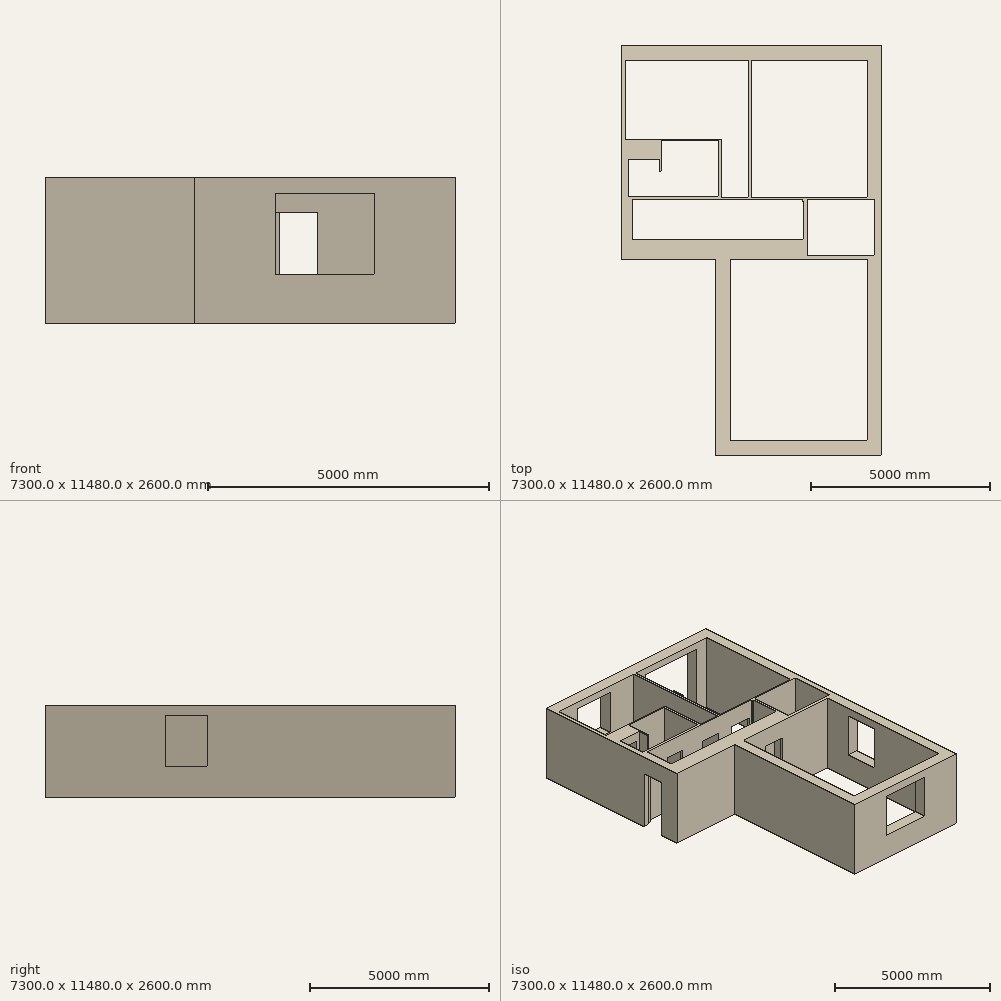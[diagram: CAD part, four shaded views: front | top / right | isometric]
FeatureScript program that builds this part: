
annotation { "Feature Type Name" : "Feature", "Feature Type Description" : "" }
export const myFeature = defineFeature(function(context is Context, id is Id, definition is map)
    precondition{}
    {
        {
            var Q0;
            Q0=qCreatedBy(makeId("Top.planeOp"),FACE);
            var sketch = newSketch(context, id + "F0", { "sketchPlane" : qUnion([Q0])});
            skLineSegment(sketch, "E0", {"start": v(-2650, 11480) * mm, "end": v(4650, 11480) * mm});
            skLineSegment(sketch, "E1", {"start": v(4650, 11480) * mm, "end": v(4650, 0) * mm});
            skLineSegment(sketch, "E2", {"start": v(4650, 0) * mm, "end": v(0, 0) * mm});
            skLineSegment(sketch, "E3", {"start": v(0, 0) * mm, "end": v(0, 5500) * mm});
            skLineSegment(sketch, "E4", {"start": v(0, 5500) * mm, "end": v(-2650, 5500) * mm});
            skLineSegment(sketch, "E5", {"start": v(-2650, 5500) * mm, "end": v(-2650, 11480) * mm});
            skLineSegment(sketch, "E6.bottom", {"start": v(4250, 410) * mm, "end": v(400, 410) * mm});
            skLineSegment(sketch, "E6.top", {"start": v(4250, 5500) * mm, "end": v(400, 5500) * mm});
            skLineSegment(sketch, "E6.left", {"start": v(4250, 410) * mm, "end": v(4250, 5500) * mm});
            skLineSegment(sketch, "E6.right", {"start": v(400, 410) * mm, "end": v(400, 5500) * mm});
            skLineSegment(sketch, "E7.bottom", {"start": v(4455, 5610) * mm, "end": v(2565, 5610) * mm});
            skLineSegment(sketch, "E7.top", {"start": v(4455, 7160) * mm, "end": v(2565, 7160) * mm});
            skLineSegment(sketch, "E7.left", {"start": v(4455, 5610) * mm, "end": v(4455, 7160) * mm});
            skLineSegment(sketch, "E7.right", {"start": v(2565, 5610) * mm, "end": v(2565, 7160) * mm});
            skLineSegment(sketch, "E8.bottom", {"start": v(-2335, 7160) * mm, "end": v(2425, 7160) * mm});
            skLineSegment(sketch, "E8.top", {"start": v(-2335, 6060) * mm, "end": v(2465, 6060) * mm});
            skLineSegment(sketch, "E8.left", {"start": v(-2335, 7160) * mm, "end": v(-2335, 6060) * mm});
            skLineSegment(sketch, "E8.right", {"start": v(2465, 7110) * mm, "end": v(2465, 6060) * mm});
            skLineSegment(sketch, "E9", {"start": v(915, 7220) * mm, "end": v(915, 11050) * mm});
            skLineSegment(sketch, "E10", {"start": v(915, 11050) * mm, "end": v(-2525, 11050) * mm});
            skLineSegment(sketch, "E11", {"start": v(-2525, 11050) * mm, "end": v(-2525, 8860) * mm});
            skLineSegment(sketch, "E12", {"start": v(-2525, 8860) * mm, "end": v(165, 8860) * mm});
            skLineSegment(sketch, "E13", {"start": v(165, 8860) * mm, "end": v(165, 7220) * mm});
            skLineSegment(sketch, "E14", {"start": v(165, 7220) * mm, "end": v(915, 7220) * mm});
            skLineSegment(sketch, "E15.bottom", {"start": v(1000, 11050) * mm, "end": v(4250, 11050) * mm});
            skLineSegment(sketch, "E15.top", {"start": v(1000, 7220) * mm, "end": v(4250, 7220) * mm});
            skLineSegment(sketch, "E15.left", {"start": v(1000, 11050) * mm, "end": v(1000, 7220) * mm});
            skLineSegment(sketch, "E15.right", {"start": v(4250, 11050) * mm, "end": v(4250, 7220) * mm});
            skLineSegment(sketch, "E16", {"start": v(-2440, 7260) * mm, "end": v(65, 7260) * mm});
            skLineSegment(sketch, "E17", {"start": v(65, 7260) * mm, "end": v(65, 8810) * mm});
            skLineSegment(sketch, "E18", {"start": v(65, 8810) * mm, "end": v(-1530, 8810) * mm});
            skLineSegment(sketch, "E19", {"start": v(-1530, 8810) * mm, "end": v(-1530, 7940) * mm});
            skLineSegment(sketch, "E20", {"start": v(-1530, 7940) * mm, "end": v(-1580, 7940) * mm});
            skLineSegment(sketch, "E21", {"start": v(-1580, 7940) * mm, "end": v(-1580, 8290) * mm});
            skLineSegment(sketch, "E22", {"start": v(-1580, 8290) * mm, "end": v(-2440, 8290) * mm});
            skLineSegment(sketch, "E23", {"start": v(-2440, 8290) * mm, "end": v(-2440, 7260) * mm});
            skLineSegment(sketch, "E24", {"start": v(2465, 7110) * mm, "end": v(2425, 7110) * mm});
            skLineSegment(sketch, "E25", {"start": v(2425, 7110) * mm, "end": v(2425, 7160) * mm});
            skSolve(sketch);
        }
        {
            var Q0;
            Q0=makeQuery(id+"F0.imprint","IMPRINT",FACE,{"disambiguationData":[TD([[makeQuery(id+"F0.imprint","IMPRINT",EDGE,{"derivedFrom":sQuery(id+"F0.wireOp",EDGE,"E0")}),-1.0]])]});
            extrude(context, id + "F1", {"entities" : qUnion([Q0]), "depth" : 2600 * mm});
        }
        {
            var Q0;
            Q0=makeQuery(id+"F1.opExtrude","SWEPT_FACE",FACE,{"disambiguationData":[OSD([sQuery(id+"F0.wireOp",EDGE,"E6.top")])]});
            var sketch = newSketch(context, id + "F2", { "sketchPlane" : qUnion([Q0])});
            skLineSegment(sketch, "E26.bottom", {"start": v(1385, 1970) * mm, "end": v(2185, 1970) * mm});
            skLineSegment(sketch, "E26.top", {"start": v(1385, 0) * mm, "end": v(2185, 0) * mm});
            skLineSegment(sketch, "E26.left", {"start": v(1385, 1970) * mm, "end": v(1385, 0) * mm});
            skLineSegment(sketch, "E26.right", {"start": v(2185, 1970) * mm, "end": v(2185, 0) * mm});
            skSolve(sketch);
        }
        {
            var Q0;
            Q0=qSketchRegion(id+"F2",true);
            extrude(context, id + "F3", {"entities" : qUnion([Q0]), "operationType" : NewBodyOperationType.REMOVE, "endBound" : BoundingType.UP_TO_NEXT, "oppositeDirection" : true, "depth" : 25 * mm});
        }
        {
            var Q0;
            Q0=makeQuery(id+"F1.opExtrude","SWEPT_FACE",FACE,{"disambiguationData":[OSD([sQuery(id+"F0.wireOp",EDGE,"E8.right")])]});
            var sketch = newSketch(context, id + "F4", { "sketchPlane" : qUnion([Q0])});
            skLineSegment(sketch, "E27.bottom", {"start": v(-6735, 0) * mm, "end": v(-6135, 0) * mm});
            skLineSegment(sketch, "E27.top", {"start": v(-6735, 1970) * mm, "end": v(-6135, 1970) * mm});
            skLineSegment(sketch, "E27.left", {"start": v(-6735, 0) * mm, "end": v(-6735, 1970) * mm});
            skLineSegment(sketch, "E27.right", {"start": v(-6135, 0) * mm, "end": v(-6135, 1970) * mm});
            skSolve(sketch);
        }
        {
            var Q0;
            Q0=qSketchRegion(id+"F4",true);
            extrude(context, id + "F5", {"entities" : qUnion([Q0]), "operationType" : NewBodyOperationType.REMOVE, "endBound" : BoundingType.UP_TO_NEXT, "oppositeDirection" : true, "depth" : 25 * mm});
        }
        {
            var Q0;
            Q0=makeQuery(id+"F1.opExtrude","SWEPT_FACE",FACE,{"disambiguationData":[OSD([sQuery(id+"F0.wireOp",EDGE,"E8.bottom")])]});
            var sketch = newSketch(context, id + "F6", { "sketchPlane" : qUnion([Q0])});
            skLineSegment(sketch, "E28.bottom", {"start": v(165, 1970) * mm, "end": v(915, 1970) * mm});
            skLineSegment(sketch, "E28.top", {"start": v(165, 0) * mm, "end": v(915, 0) * mm});
            skLineSegment(sketch, "E28.left", {"start": v(165, 1970) * mm, "end": v(165, 0) * mm});
            skLineSegment(sketch, "E28.right", {"start": v(915, 1970) * mm, "end": v(915, 0) * mm});
            skSolve(sketch);
        }
        {
            var Q0;
            Q0=makeQuery(id+"F6.imprint","IMPRINT",FACE,{"disambiguationData":[TD([[makeQuery(id+"F6.imprint","IMPRINT",EDGE,{"derivedFrom":sQuery(id+"F6.wireOp",EDGE,"E28.bottom")}),-1.0]])]});
            extrude(context, id + "F7", {"entities" : qUnion([Q0]), "operationType" : NewBodyOperationType.REMOVE, "endBound" : BoundingType.UP_TO_NEXT, "oppositeDirection" : true, "depth" : 25 * mm});
        }
        {
            var Q0;
            Q0=makeQuery(id+"F1.opExtrude","SWEPT_FACE",FACE,{"disambiguationData":[OSD([sQuery(id+"F0.wireOp",EDGE,"E8.bottom")])]});
            var sketch = newSketch(context, id + "F8", { "sketchPlane" : qUnion([Q0])});
            skLineSegment(sketch, "E29.bottom", {"start": v(1515, 1967.95) * mm, "end": v(2315, 1967.95) * mm});
            skLineSegment(sketch, "E29.top", {"start": v(1515, -2.05) * mm, "end": v(2315, -2.05) * mm});
            skLineSegment(sketch, "E29.left", {"start": v(1515, 1967.95) * mm, "end": v(1515, -2.05) * mm});
            skLineSegment(sketch, "E29.right", {"start": v(2315, 1967.95) * mm, "end": v(2315, -2.05) * mm});
            skSolve(sketch);
        }
        {
            var Q0;
            {var subQ8=sQuery(id+"F8.wireOp",EDGE,"E29.bottom");Q0=makeQuery(id+"F8.imprint","IMPRINT",FACE,{"disambiguationData":[TD([[makeQuery(id+"F8.imprint","IMPRINT",EDGE,{"derivedFrom":subQ8}),-1.0]])]});}
            extrude(context, id + "F9", {"entities" : qUnion([Q0]), "operationType" : NewBodyOperationType.REMOVE, "endBound" : BoundingType.UP_TO_NEXT, "oppositeDirection" : true, "depth" : 25 * mm});
        }
        {
            var Q0;
            Q0=makeQuery(id+"F1.opExtrude","SWEPT_FACE",FACE,{"disambiguationData":[OSD([sQuery(id+"F0.wireOp",EDGE,"E2")])]});
            var sketch = newSketch(context, id + "F10", { "sketchPlane" : qUnion([Q0])});
            skLineSegment(sketch, "E30.bottom", {"start": v(1450, 2320) * mm, "end": v(3200, 2320) * mm});
            skLineSegment(sketch, "E30.top", {"start": v(1450, 870) * mm, "end": v(3200, 870) * mm});
            skLineSegment(sketch, "E30.left", {"start": v(1450, 2320) * mm, "end": v(1450, 870) * mm});
            skLineSegment(sketch, "E30.right", {"start": v(3200, 2320) * mm, "end": v(3200, 870) * mm});
            skSolve(sketch);
        }
        {
            var Q0;
            Q0=qSketchRegion(id+"F10",true);
            extrude(context, id + "F11", {"entities" : qUnion([Q0]), "operationType" : NewBodyOperationType.REMOVE, "endBound" : BoundingType.UP_TO_NEXT, "oppositeDirection" : true, "depth" : 25 * mm});
        }
        {
            var Q0;
            Q0=makeQuery(id+"F1.opExtrude","SWEPT_FACE",FACE,{"disambiguationData":[OSD([sQuery(id+"F0.wireOp",EDGE,"E1")])]});
            var sketch = newSketch(context, id + "F12", { "sketchPlane" : qUnion([Q0])});
            skLineSegment(sketch, "E31.bottom", {"start": v(3362.5, 2320) * mm, "end": v(4537.5, 2320) * mm});
            skLineSegment(sketch, "E31.top", {"start": v(3362.5, 870) * mm, "end": v(4537.5, 870) * mm});
            skLineSegment(sketch, "E31.left", {"start": v(3362.5, 2320) * mm, "end": v(3362.5, 870) * mm});
            skLineSegment(sketch, "E31.right", {"start": v(4537.5, 2320) * mm, "end": v(4537.5, 870) * mm});
            skSolve(sketch);
        }
        {
            var Q0;
            Q0=makeQuery(id+"F12.imprint","IMPRINT",FACE,{"disambiguationData":[TD([[makeQuery(id+"F12.imprint","IMPRINT",EDGE,{"derivedFrom":sQuery(id+"F12.wireOp",EDGE,"E31.bottom")}),-1.0]])]});
            extrude(context, id + "F13", {"entities" : qUnion([Q0]), "operationType" : NewBodyOperationType.REMOVE, "endBound" : BoundingType.UP_TO_NEXT, "oppositeDirection" : true, "depth" : 25 * mm});
        }
        {
            var Q0;
            Q0=makeQuery(id+"F1.opExtrude","SWEPT_FACE",FACE,{"disambiguationData":[OSD([sQuery(id+"F0.wireOp",EDGE,"E0")])]});
            var sketch = newSketch(context, id + "F14", { "sketchPlane" : qUnion([Q0])});
            skLineSegment(sketch, "E32", {"start": v(-3800, 0) * mm, "end": v(-3800, 2340) * mm});
            skLineSegment(sketch, "E33", {"start": v(-3800, 2340) * mm, "end": v(-1450, 2340) * mm});
            skLineSegment(sketch, "E34", {"start": v(-1450, 2340) * mm, "end": v(-1450, 870) * mm});
            skLineSegment(sketch, "E35", {"start": v(-1450, 870) * mm, "end": v(-3200, 870) * mm});
            skLineSegment(sketch, "E36", {"start": v(-3200, 870) * mm, "end": v(-3200, 0) * mm});
            skSolve(sketch);
        }
        {
            var Q0;
            {var subQ2=sQuery(id+"F14.wireOp",EDGE,"E32");Q0=makeQuery(id+"F14.imprint","IMPRINT",FACE,{"disambiguationData":[TD([[makeQuery(id+"F14.imprint","IMPRINT",EDGE,{"derivedFrom":subQ2}),-1.0]])]});}
            extrude(context, id + "F15", {"entities" : qUnion([Q0]), "operationType" : NewBodyOperationType.REMOVE, "endBound" : BoundingType.UP_TO_NEXT, "oppositeDirection" : true, "depth" : 25 * mm});
        }
        {
            var Q0;
            Q0=makeQuery(id+"F1.opExtrude","SWEPT_FACE",FACE,{"disambiguationData":[OSD([sQuery(id+"F0.wireOp",EDGE,"E0")])]});
            var sketch = newSketch(context, id + "F16", { "sketchPlane" : qUnion([Q0])});
            skLineSegment(sketch, "E37.bottom", {"start": v(160, 2340) * mm, "end": v(1660, 2340) * mm});
            skLineSegment(sketch, "E37.top", {"start": v(160, 870) * mm, "end": v(1660, 870) * mm});
            skLineSegment(sketch, "E37.left", {"start": v(160, 2340) * mm, "end": v(160, 870) * mm});
            skLineSegment(sketch, "E37.right", {"start": v(1660, 2340) * mm, "end": v(1660, 870) * mm});
            skSolve(sketch);
        }
        {
            var Q0;
            Q0=makeQuery(id+"F16.imprint","IMPRINT",FACE,{"disambiguationData":[TD([[makeQuery(id+"F16.imprint","IMPRINT",EDGE,{"derivedFrom":sQuery(id+"F16.wireOp",EDGE,"E37.bottom")}),-1.0]])]});
            extrude(context, id + "F17", {"entities" : qUnion([Q0]), "operationType" : NewBodyOperationType.REMOVE, "endBound" : BoundingType.UP_TO_NEXT, "oppositeDirection" : true, "depth" : 25 * mm});
        }
        {
            var Q0;
            Q0=makeQuery(id+"F1.opExtrude","SWEPT_FACE",FACE,{"disambiguationData":[OSD([sQuery(id+"F0.wireOp",EDGE,"E8.top")])]});
            var sketch = newSketch(context, id + "F18", { "sketchPlane" : qUnion([Q0])});
            skLineSegment(sketch, "E38", {"start": v(-2465, 2350) * mm, "end": v(-1315, 2350) * mm});
            skLineSegment(sketch, "E39", {"start": v(-1315, 2350) * mm, "end": v(-1315, 0) * mm});
            skSolve(sketch);
        }
        {
            var Q0;
            {var subQ11=sQuery(id+"F18.wireOp",EDGE,"E38");Q0=makeQuery(id+"F18.imprint","IMPRINT",FACE,{"disambiguationData":[TD([[makeQuery(id+"F18.imprint","IMPRINT",EDGE,{"derivedFrom":subQ11}),-1.0]])]});}
            extrude(context, id + "F19", {"entities" : qUnion([Q0]), "operationType" : NewBodyOperationType.REMOVE, "oppositeDirection" : true, "depth" : 460 * mm});
        }
        {
            var Q0;
            Q0=makeQuery(id+"F1.opExtrude","CAP_FACE",FACE,{"disambiguationData":[OSD([sQuery(id+"F0.wireOp",EDGE,"E0"),sQuery(id+"F0.wireOp",EDGE,"E1"),sQuery(id+"F0.wireOp",EDGE,"E2"),sQuery(id+"F0.wireOp",EDGE,"E3"),sQuery(id+"F0.wireOp",EDGE,"E4"),sQuery(id+"F0.wireOp",EDGE,"E5"),sQuery(id+"F0.wireOp",EDGE,"E6.bottom"),sQuery(id+"F0.wireOp",EDGE,"E6.top"),sQuery(id+"F0.wireOp",EDGE,"E6.left"),sQuery(id+"F0.wireOp",EDGE,"E6.right"),sQuery(id+"F0.wireOp",EDGE,"E7.bottom"),sQuery(id+"F0.wireOp",EDGE,"E7.top"),sQuery(id+"F0.wireOp",EDGE,"E7.left"),sQuery(id+"F0.wireOp",EDGE,"E7.right"),sQuery(id+"F0.wireOp",EDGE,"E8.bottom"),sQuery(id+"F0.wireOp",EDGE,"E8.top"),sQuery(id+"F0.wireOp",EDGE,"E8.left"),sQuery(id+"F0.wireOp",EDGE,"E8.right"),sQuery(id+"F0.wireOp",EDGE,"E9"),sQuery(id+"F0.wireOp",EDGE,"E10"),sQuery(id+"F0.wireOp",EDGE,"E11"),sQuery(id+"F0.wireOp",EDGE,"E12"),sQuery(id+"F0.wireOp",EDGE,"E13"),sQuery(id+"F0.wireOp",EDGE,"E14"),sQuery(id+"F0.wireOp",EDGE,"E15.bottom"),sQuery(id+"F0.wireOp",EDGE,"E15.top"),sQuery(id+"F0.wireOp",EDGE,"E15.left"),sQuery(id+"F0.wireOp",EDGE,"E15.right"),sQuery(id+"F0.wireOp",EDGE,"E16"),sQuery(id+"F0.wireOp",EDGE,"E17"),sQuery(id+"F0.wireOp",EDGE,"E18"),sQuery(id+"F0.wireOp",EDGE,"E19"),sQuery(id+"F0.wireOp",EDGE,"E20"),sQuery(id+"F0.wireOp",EDGE,"E21"),sQuery(id+"F0.wireOp",EDGE,"E22"),sQuery(id+"F0.wireOp",EDGE,"E23"),sQuery(id+"F0.wireOp",EDGE,"E24"),sQuery(id+"F0.wireOp",EDGE,"E25")])],"isStart":true});
            var sketch = newSketch(context, id + "F20", { "sketchPlane" : qUnion([Q0])});
            skLineSegment(sketch, "E40", {"start": v(325, -6060) * mm, "end": v(325, -5650) * mm});
            skLineSegment(sketch, "E41", {"start": v(325, -5650) * mm, "end": v(-640, -5650) * mm});
            skLineSegment(sketch, "E42", {"start": v(-640, -5650) * mm, "end": v(-640, -6060) * mm});
            skSolve(sketch);
        }
        {
            var Q0;
            {var subQ4=sQuery(id+"F20.wireOp",EDGE,"E40");Q0=makeQuery(id+"F20.imprint","IMPRINT",FACE,{"disambiguationData":[TD([[makeQuery(id+"F20.imprint","IMPRINT",EDGE,{"derivedFrom":subQ4}),1.0]])]});}
            extrude(context, id + "F21", {"entities" : qUnion([Q0]), "operationType" : NewBodyOperationType.REMOVE, "oppositeDirection" : true, "depth" : 2355 * mm});
        }
        {
            var Q0;
            Q0=makeQuery(id+"F1.opExtrude","CAP_FACE",FACE,{"disambiguationData":[OSD([sQuery(id+"F0.wireOp",EDGE,"E0"),sQuery(id+"F0.wireOp",EDGE,"E1"),sQuery(id+"F0.wireOp",EDGE,"E2"),sQuery(id+"F0.wireOp",EDGE,"E3"),sQuery(id+"F0.wireOp",EDGE,"E4"),sQuery(id+"F0.wireOp",EDGE,"E5"),sQuery(id+"F0.wireOp",EDGE,"E6.bottom"),sQuery(id+"F0.wireOp",EDGE,"E6.top"),sQuery(id+"F0.wireOp",EDGE,"E6.left"),sQuery(id+"F0.wireOp",EDGE,"E6.right"),sQuery(id+"F0.wireOp",EDGE,"E7.bottom"),sQuery(id+"F0.wireOp",EDGE,"E7.top"),sQuery(id+"F0.wireOp",EDGE,"E7.left"),sQuery(id+"F0.wireOp",EDGE,"E7.right"),sQuery(id+"F0.wireOp",EDGE,"E8.bottom"),sQuery(id+"F0.wireOp",EDGE,"E8.top"),sQuery(id+"F0.wireOp",EDGE,"E8.left"),sQuery(id+"F0.wireOp",EDGE,"E8.right"),sQuery(id+"F0.wireOp",EDGE,"E9"),sQuery(id+"F0.wireOp",EDGE,"E10"),sQuery(id+"F0.wireOp",EDGE,"E11"),sQuery(id+"F0.wireOp",EDGE,"E12"),sQuery(id+"F0.wireOp",EDGE,"E13"),sQuery(id+"F0.wireOp",EDGE,"E14"),sQuery(id+"F0.wireOp",EDGE,"E15.bottom"),sQuery(id+"F0.wireOp",EDGE,"E15.top"),sQuery(id+"F0.wireOp",EDGE,"E15.left"),sQuery(id+"F0.wireOp",EDGE,"E15.right"),sQuery(id+"F0.wireOp",EDGE,"E16"),sQuery(id+"F0.wireOp",EDGE,"E17"),sQuery(id+"F0.wireOp",EDGE,"E18"),sQuery(id+"F0.wireOp",EDGE,"E19"),sQuery(id+"F0.wireOp",EDGE,"E20"),sQuery(id+"F0.wireOp",EDGE,"E21"),sQuery(id+"F0.wireOp",EDGE,"E22"),sQuery(id+"F0.wireOp",EDGE,"E23"),sQuery(id+"F0.wireOp",EDGE,"E24"),sQuery(id+"F0.wireOp",EDGE,"E25")])],"isStart":true});
            var sketch = newSketch(context, id + "F22", { "sketchPlane" : qUnion([Q0])});
            skLineSegment(sketch, "E43", {"start": v(-735, -6060) * mm, "end": v(-735, -5715) * mm});
            skLineSegment(sketch, "E44", {"start": v(-735, -5715) * mm, "end": v(-1900, -5715) * mm});
            skLineSegment(sketch, "E45", {"start": v(-1900, -5715) * mm, "end": v(-1900, -6060) * mm});
            skSolve(sketch);
        }
        {
            var Q0;
            {var subQ7=sQuery(id+"F22.wireOp",EDGE,"E43");Q0=makeQuery(id+"F22.imprint","IMPRINT",FACE,{"disambiguationData":[TD([[makeQuery(id+"F22.imprint","IMPRINT",EDGE,{"derivedFrom":subQ7}),1.0]])]});}
            extrude(context, id + "F23", {"entities" : qUnion([Q0]), "operationType" : NewBodyOperationType.REMOVE, "oppositeDirection" : true, "depth" : 2355 * mm});
        }
        {
            var Q0;
            Q0=makeQuery(id+"F1.opExtrude","SWEPT_FACE",FACE,{"disambiguationData":[OSD([sQuery(id+"F0.wireOp",EDGE,"E8.left")])]});
            var sketch = newSketch(context, id + "F24", { "sketchPlane" : qUnion([Q0])});
            skLineSegment(sketch, "E46.bottom", {"start": v(6210, 0) * mm, "end": v(7010, 0) * mm});
            skLineSegment(sketch, "E46.top", {"start": v(6210, 1970) * mm, "end": v(7010, 1970) * mm});
            skLineSegment(sketch, "E46.left", {"start": v(6210, 0) * mm, "end": v(6210, 1970) * mm});
            skLineSegment(sketch, "E46.right", {"start": v(7010, 0) * mm, "end": v(7010, 1970) * mm});
            skSolve(sketch);
        }
        {
            var Q0;
            Q0=makeQuery(id+"F24.imprint","IMPRINT",FACE,{"disambiguationData":[TD([[makeQuery(id+"F24.imprint","IMPRINT",EDGE,{"derivedFrom":sQuery(id+"F24.wireOp",EDGE,"E46.bottom")}),-1.0]])]});
            extrude(context, id + "F25", {"entities" : qUnion([Q0]), "operationType" : NewBodyOperationType.REMOVE, "endBound" : BoundingType.UP_TO_NEXT, "oppositeDirection" : true, "depth" : 25 * mm});
        }
        {
            var Q0;
            Q0=makeQuery(id+"F1.opExtrude","SWEPT_FACE",FACE,{"disambiguationData":[OSD([sQuery(id+"F0.wireOp",EDGE,"E8.left")])]});
            var sketch = newSketch(context, id + "F26", { "sketchPlane" : qUnion([Q0])});
            skLineSegment(sketch, "E47", {"start": v(6060, 2355) * mm, "end": v(7050, 2355) * mm});
            skLineSegment(sketch, "E48", {"start": v(7050, 2355) * mm, "end": v(7050, 0) * mm});
            skSolve(sketch);
        }
        {
            var Q0;
            {var subQ13=sQuery(id+"F26.wireOp",EDGE,"E47");Q0=makeQuery(id+"F26.imprint","IMPRINT",FACE,{"disambiguationData":[TD([[makeQuery(id+"F26.imprint","IMPRINT",EDGE,{"derivedFrom":subQ13}),-1.0]])]});}
            extrude(context, id + "F27", {"entities" : qUnion([Q0]), "operationType" : NewBodyOperationType.REMOVE, "oppositeDirection" : true, "depth" : 115 * mm});
        }
        {
            var Q0;
            Q0=makeQuery(id+"F1.opExtrude","SWEPT_FACE",FACE,{"disambiguationData":[OSD([sQuery(id+"F0.wireOp",EDGE,"E8.bottom")])]});
            var sketch = newSketch(context, id + "F28", { "sketchPlane" : qUnion([Q0])});
            skLineSegment(sketch, "E49", {"start": v(-740, 0) * mm, "end": v(-740, 2000) * mm});
            skLineSegment(sketch, "E50", {"start": v(-740, 2000) * mm, "end": v(-1440, 2000) * mm});
            skLineSegment(sketch, "E51", {"start": v(-1440, 2000) * mm, "end": v(-1440, 0) * mm});
            skSolve(sketch);
        }
        {
            var Q0;
            {var subQ5=sQuery(id+"F28.wireOp",EDGE,"E49");Q0=makeQuery(id+"F28.imprint","IMPRINT",FACE,{"disambiguationData":[TD([[makeQuery(id+"F28.imprint","IMPRINT",EDGE,{"derivedFrom":subQ5}),1.0]])]});}
            extrude(context, id + "F29", {"entities" : qUnion([Q0]), "operationType" : NewBodyOperationType.REMOVE, "endBound" : BoundingType.UP_TO_NEXT, "oppositeDirection" : true, "depth" : 25 * mm});
        }
        {
            var Q0;
            Q0=makeQuery(id+"F1.opExtrude","SWEPT_FACE",FACE,{"disambiguationData":[OSD([sQuery(id+"F0.wireOp",EDGE,"E22")])]});
            var sketch = newSketch(context, id + "F30", { "sketchPlane" : qUnion([Q0])});
            skLineSegment(sketch, "E52.bottom", {"start": v(-2285.5, 2290) * mm, "end": v(-1705.5, 2290) * mm});
            skLineSegment(sketch, "E52.top", {"start": v(-2285.5, 1700) * mm, "end": v(-1705.5, 1700) * mm});
            skLineSegment(sketch, "E52.left", {"start": v(-2285.5, 2290) * mm, "end": v(-2285.5, 1700) * mm});
            skLineSegment(sketch, "E52.right", {"start": v(-1705.5, 2290) * mm, "end": v(-1705.5, 1700) * mm});
            skSolve(sketch);
        }
        {
            var Q0;
            Q0=qSketchRegion(id+"F30",true);
            extrude(context, id + "F31", {"entities" : qUnion([Q0]), "operationType" : NewBodyOperationType.REMOVE, "oppositeDirection" : true, "depth" : 300 * mm});
        }
    });
